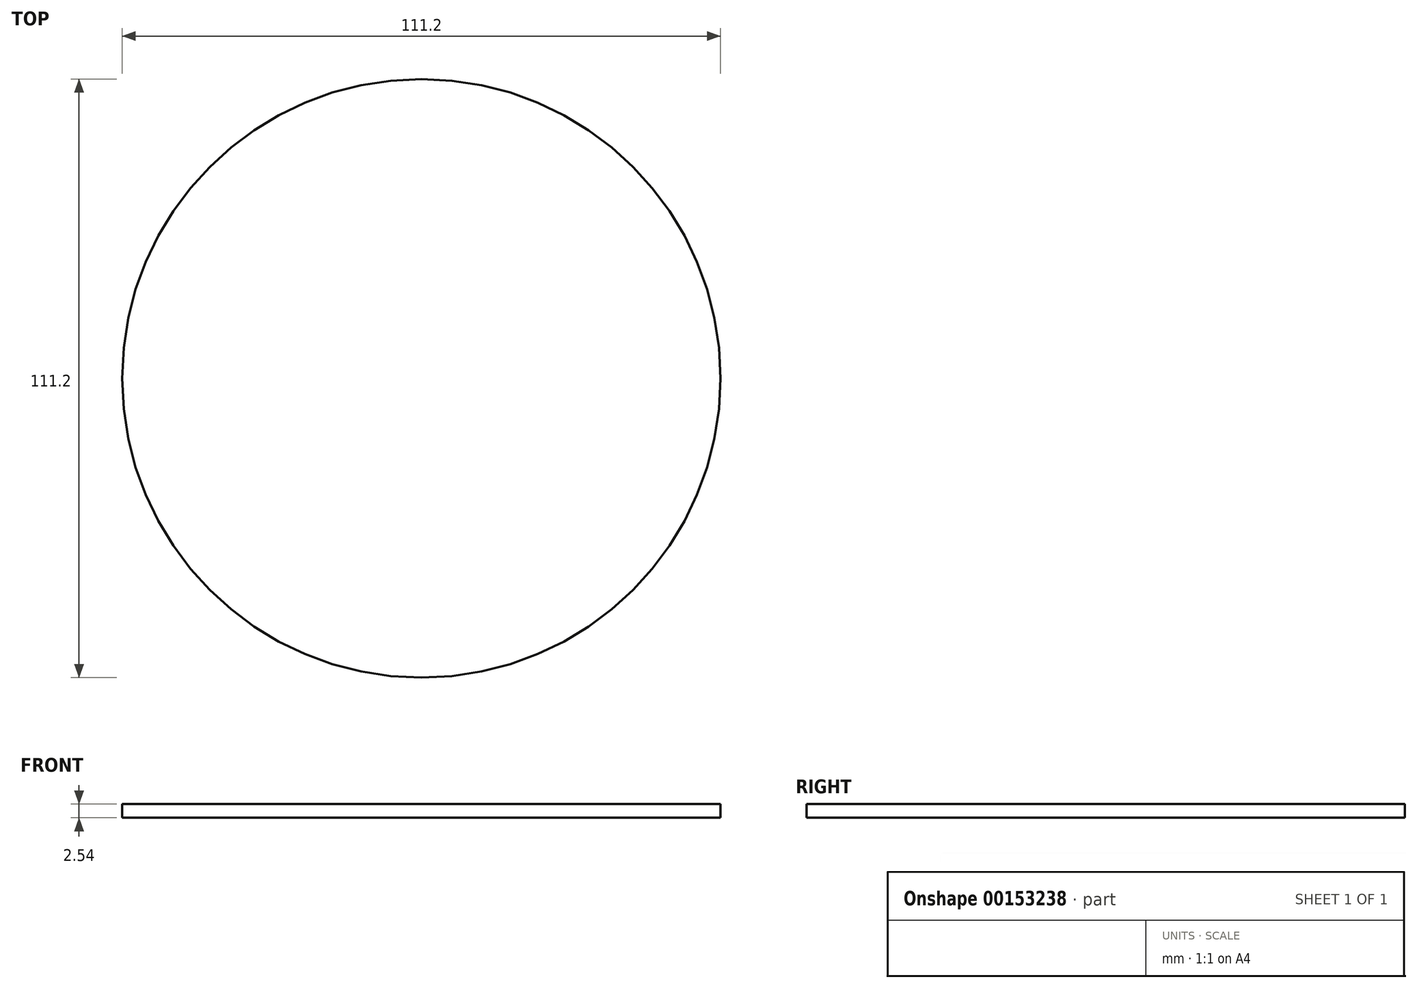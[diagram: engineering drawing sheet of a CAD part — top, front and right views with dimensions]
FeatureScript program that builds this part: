
annotation { "Feature Type Name" : "Feature", "Feature Type Description" : "" }
export const myFeature = defineFeature(function(context is Context, id is Id, definition is map)
    precondition{}
    {
        {
            var Q0;
            Q0=qCreatedBy(makeId("Top.planeOp"),FACE);
            var sketch = newSketch(context, id + "F0", { "sketchPlane" : qUnion([Q0])});
            skCircle(sketch, "E0", {"center": v(0, 0) * mm, "radius": 55.6 * mm});
            skSolve(sketch);
        }
        {
            var Q0;
            Q0 = qSketchRegion(id + "F0", true);
            extrude(context, id + "F1", {"entities" : qUnion([Q0]), "depth" : 2.54 * mm});
        }
    });
